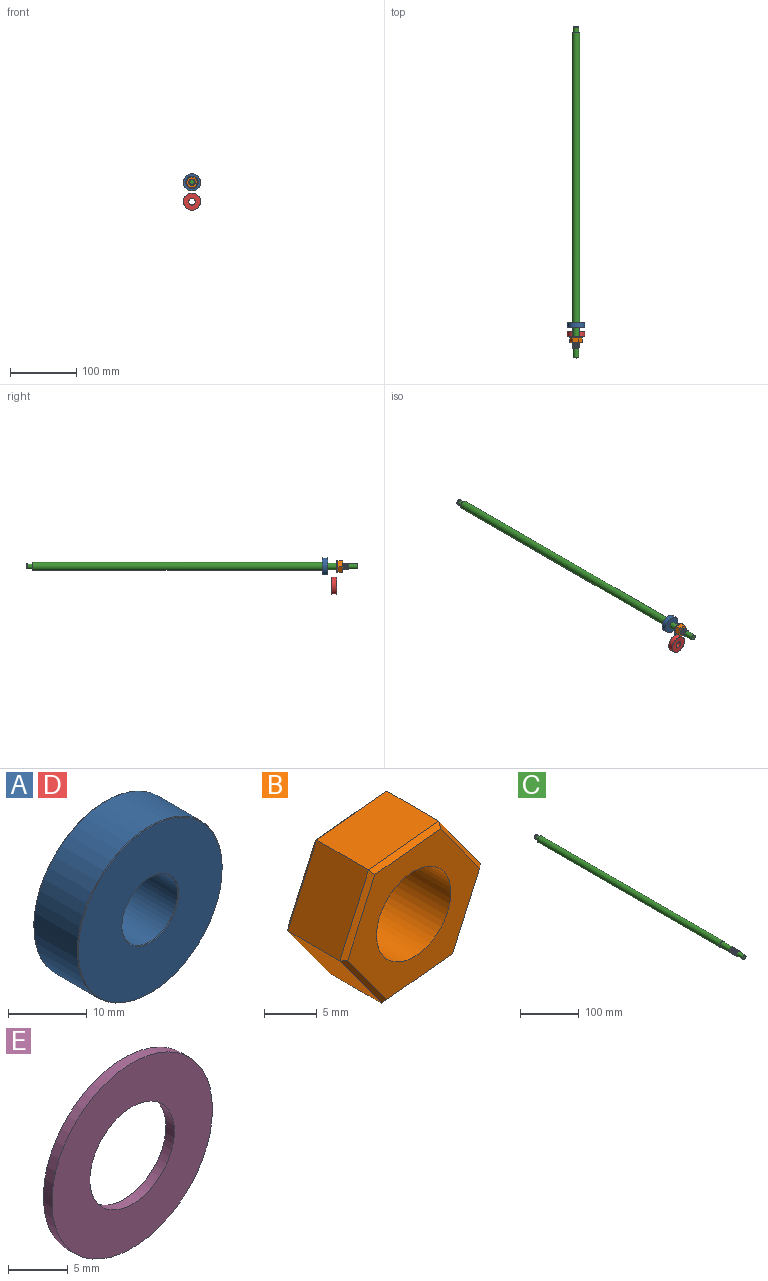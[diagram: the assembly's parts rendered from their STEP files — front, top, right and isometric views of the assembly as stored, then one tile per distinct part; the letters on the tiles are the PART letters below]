
ASSEMBLY  parts=5 mates=1
PART A: 8 faces, bbox 26x8x26 mm
  f0: cylinder r=5mm len=10mm, axis (0,1,0), area 245mm2, adj f6,f7
  f1: cylinder r=13mm len=26mm, axis (0,1,0), area 637.1mm2, adj f4,f5
  f2: plane 25.8x25.8mm, normal (0,-1,0), area 441.1mm2, adj f5,f7
  f3: plane 25.8x25.8mm, normal (0,1,0), area 441.1mm2, adj f4,f6
  f4: cone r=13mm half-angle=45deg, axis (0,-1,0), area 11.5mm2, adj f1,f3
  f5: cone r=12.9mm half-angle=45deg, axis (0,1,0), area 11.5mm2, adj f1,f2
  f6: cone r=5.1mm half-angle=45deg, axis (0,1,0), area 4.5mm2, adj f0,f3
  f7: cone r=5mm half-angle=45deg, axis (0,-1,0), area 4.5mm2, adj f0,f2
PART B: 21 faces, bbox 18.9x8x17.3 mm
  f0: plane 7.69x7mm, normal (0.81,0,0.59), area 66.5mm2, adj f1,f5,f12,f17
  f1: plane 9.45x7mm, normal (-0.1,0,0.99), area 66.5mm2, adj f0,f2,f10,f19
  f2: plane 8.67x7mm, normal (-0.91,0,0.41), area 66.5mm2, adj f1,f3,f9,f20
  f3: plane 7.69x7mm, normal (-0.81,0,-0.59), area 66.5mm2, adj f2,f4,f11,f18
  f4: plane 9.45x7mm, normal (0.1,0,-0.99), area 66.5mm2, adj f3,f5,f13,f16
  f5: plane 8.67x7mm, normal (0.91,0,-0.41), area 66.5mm2, adj f0,f4,f14,f15
  f6: cylinder r=5mm len=10mm, axis (0,1,0), area 251.3mm2, adj f7,f8
  f7: plane 17.75x16.3mm, normal (0,-1,0), area 128.3mm2, adj f6,f9,f10,f11,f12,f13,f14
  f8: plane 17.75x16.3mm, normal (0,1,0), area 128.3mm2, adj f6,f15,f16,f17,f18,f19,f20
  f9: plane 8.67x4.21mm, normal (-0.65,-0.71,0.29), area 6.5mm2, adj f2,f7,f10,f11
  f10: plane 9.45x1.45mm, normal (-0.07,-0.71,0.7), area 6.5mm2, adj f1,f7,f9,f12
  f11: plane 7.75x5.81mm, normal (-0.57,-0.71,-0.41), area 6.5mm2, adj f3,f7,f9,f13
  f12: plane 7.75x5.81mm, normal (0.57,-0.71,0.41), area 6.5mm2, adj f0,f7,f10,f14
  f13: plane 9.45x1.45mm, normal (0.07,-0.71,-0.7), area 6.5mm2, adj f4,f7,f11,f14
  f14: plane 8.67x4.21mm, normal (0.65,-0.71,-0.29), area 6.5mm2, adj f5,f7,f12,f13
  f15: plane 8.67x4.21mm, normal (0.65,0.71,-0.29), area 6.5mm2, adj f5,f8,f16,f17
  f16: plane 9.45x1.45mm, normal (0.07,0.71,-0.7), area 6.5mm2, adj f4,f8,f15,f18
  f17: plane 7.75x5.81mm, normal (0.57,0.71,0.41), area 6.5mm2, adj f0,f8,f15,f19
  f18: plane 7.75x5.81mm, normal (-0.57,0.71,-0.41), area 6.5mm2, adj f3,f8,f16,f20
  f19: plane 9.45x1.45mm, normal (-0.07,0.71,0.7), area 6.5mm2, adj f1,f8,f17,f20
  f20: plane 8.67x4.21mm, normal (-0.65,0.71,0.29), area 6.5mm2, adj f2,f8,f18,f19
PART C: 40 faces, bbox 12.2x503.2x12.2 mm
  f0: plane 1.54x0.24mm, normal (0,1,0), area 0.2mm2, adj f17,f20,f31
  f1: cylinder r=5mm len=10mm, axis (0,1,0), area 3.2mm2, adj f2,f17,f21,f23
  f2: cylinder r=5mm len=10mm, axis (0,1,0), area 3.1mm2, adj f1,f3,f21,f23
  f3: cylinder r=5mm len=10mm, axis (0,1,0), area 3.1mm2, adj f2,f4,f21,f23
  f4: cylinder r=5mm len=10mm, axis (0,1,0), area 3.2mm2, adj f3,f5,f21,f23
  f5: cylinder r=5mm len=10mm, axis (0,1,0), area 3.2mm2, adj f4,f6,f21,f23
  f6: cylinder r=5mm len=10mm, axis (0,1,0), area 3.1mm2, adj f5,f7,f21,f23
  f7: cylinder r=5mm len=10mm, axis (0,1,0), area 3.1mm2, adj f6,f8,f21,f23
  f8: cylinder r=5mm len=10mm, axis (0,1,0), area 3.1mm2, adj f7,f9,f21,f23
  f9: cylinder r=5mm len=10mm, axis (0,1,0), area 3.2mm2, adj f8,f10,f21,f23
  f10: cylinder r=5mm len=10mm, axis (0,1,0), area 3.1mm2, adj f9,f11,f21,f23
  f11: cylinder r=5mm len=10mm, axis (0,1,0), area 3.1mm2, adj f10,f12,f21,f23
  f12: cylinder r=5mm len=10mm, axis (0,1,0), area 3.1mm2, adj f11,f13,f21,f23
  f13: cylinder r=5mm len=10mm, axis (0,1,0), area 3.1mm2, adj f12,f14,f21,f23
  f14: cylinder r=5mm len=10mm, axis (0,1,0), area 3.1mm2, adj f13,f15,f21,f23
  f15: cylinder r=5mm len=10mm, axis (0,1,0), area 3.1mm2, adj f14,f16,f21,f23
  f16: cylinder r=5mm len=2.92mm, axis (0,1,0), area 0.2mm2, adj f15,f19,f23
  f17: cylinder r=5mm len=23.86mm, axis (0,1,0), area 733.8mm2, adj f0,f1,f20,f21,f30,f31
  f18: plane 9.58x9.45mm, normal (0,-1,0), area 17.9mm2, adj f19,f21,f22,f23,f24,f25
  f19: cone r=4.86mm half-angle=45deg, axis (0,1,0), area 1.3mm2, adj f16,f18,f22,f23
  f20: plane 0.78x0.6mm, normal (-1,0,0), area 0.3mm2, adj f0,f17,f21,f23,f24
  f21: bspline ~16.28x11.55mm, area 264.5mm2, adj f1,f2,f3,f4,f5,f6,f7,f8
  f22: plane 0.24x0.14mm, normal (1,0,0), area 0mm2, adj f18,f19,f21
  f23: bspline ~15.94x11.55mm, area 254.2mm2, adj f1,f2,f3,f4,f5,f6,f7,f8
  f24: bspline ~16.35x10.44mm, area 184.1mm2, adj f18,f20,f21,f23
  f25: cylinder r=4mm len=14.86mm, axis (0,1,0), area 373.5mm2, adj f18,f27
  f26: plane 7.72x7.72mm, normal (0,-1,0), area 46.8mm2, adj f27
  f27: cone r=3.86mm half-angle=45deg, axis (0,1,0), area 4.9mm2, adj f25,f26
  f28: cylinder r=6mm len=438.86mm, axis (0,-1,0), area 16544.6mm2, adj f30,f33
  f29: plane 11.72x11.72mm, normal (0,1,0), area 57.6mm2, adj f32,f33
  f30: plane 12x12mm, normal (0,-1,0), area 34.6mm2, adj f17,f28
  f31: plane 1.61x0.31mm, normal (0,-0.87,0.5), area 0.3mm2, adj f0,f17,f21
  f32: cylinder r=4mm len=8mm, axis (0,-1,0), area 178.4mm2, adj f29,f35
  f33: cone r=6mm half-angle=45deg, axis (0,-1,0), area 7.4mm2, adj f28,f29
  f34: plane 8x8mm, normal (0,-1,0), area 4.9mm2, adj f36,f39
  f35: plane 8x8mm, normal (0,1,0), area 4.9mm2, adj f32,f36
  f36: cylinder r=3.8mm len=7.6mm, axis (0,1,0), area 21.5mm2, adj f34,f35
  f37: plane 7.72x7.72mm, normal (0,1,0), area 46.8mm2, adj f38
  f38: cone r=3.86mm half-angle=45deg, axis (0,-1,0), area 4.9mm2, adj f37,f39
  f39: cylinder r=4mm len=8mm, axis (0,-1,0), area 46.7mm2, adj f34,f38
PART D: same geometry as A
PART E: 4 faces, bbox 19x1x19 mm
  f0: cylinder r=5mm len=10mm, axis (0,1,0), area 31.4mm2, adj f2,f3
  f1: cylinder r=9.5mm len=19mm, axis (0,1,0), area 59.7mm2, adj f2,f3
  f2: plane 19x19mm, normal (0,-1,0), area 205mm2, adj f0,f1
  f3: plane 19x19mm, normal (0,1,0), area 205mm2, adj f0,f1
PLACE A t=(-155.24,-258.93,105.93)mm
PLACE B t=(-190.51,-281.93,148.82)mm
PLACE C t=(-155.24,-258.93,105.93)mm
PLACE D rot(axis=(1,0,0),180deg) t=(-155.24,-280.93,76.66)mm
PLACE E rot(axis=(1,0,0),180deg) t=(-156.54,-281.93,61.21)mm
MATE revolute A.f0 <-> C.f1  axis (0,-1,0) through (-155.24,-258.93,105.93)mm
